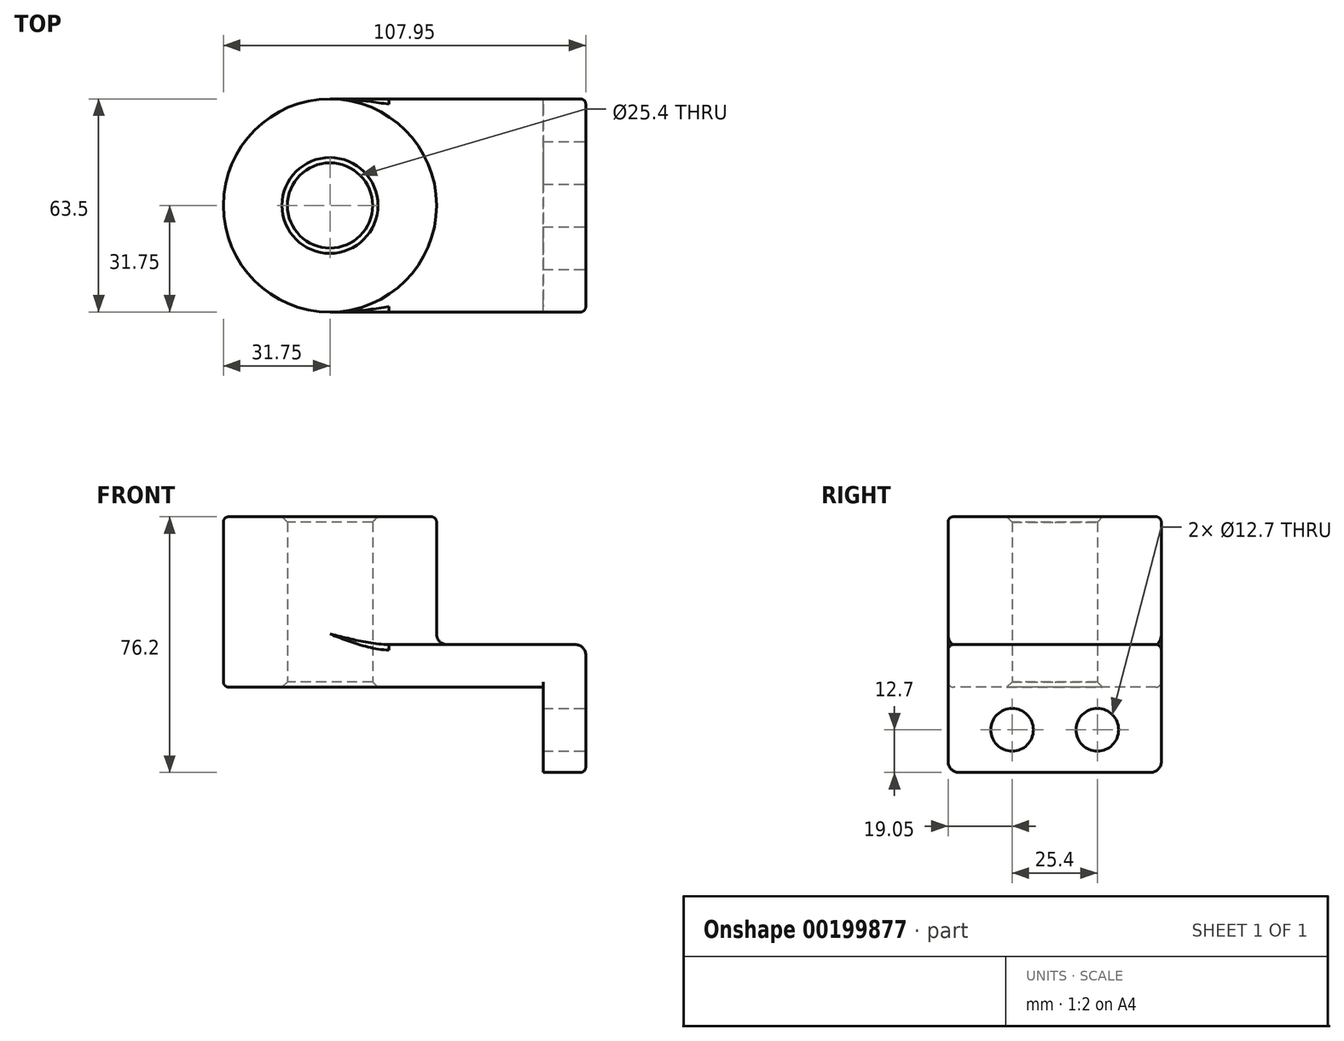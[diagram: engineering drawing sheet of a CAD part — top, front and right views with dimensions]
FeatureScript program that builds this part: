
annotation { "Feature Type Name" : "Feature", "Feature Type Description" : "" }
export const myFeature = defineFeature(function(context is Context, id is Id, definition is map)
    precondition{}
    {
        {
            var Q0;
            Q0=qCreatedBy(makeId("Top.planeOp"),FACE);
            var sketch = newSketch(context, id + "F0", { "sketchPlane" : qUnion([Q0])});
            skLineSegment(sketch, "E0.bottom", {"start": v(38.1, 31.75) * mm, "end": v(-38.1, 31.75) * mm});
            skLineSegment(sketch, "E0.top", {"start": v(38.1, -31.75) * mm, "end": v(-38.1, -31.75) * mm});
            skLineSegment(sketch, "E0.left", {"start": v(38.1, 31.75) * mm, "end": v(38.1, -31.75) * mm});
            skLineSegment(sketch, "E0.right", {"start": v(-38.1, 31.75) * mm, "end": v(-38.1, -31.75) * mm});
            skPoint(sketch, "E0.middle", {"position": v(0, 0) * mm});
            skCircle(sketch, "E1", {"center": v(-38.1, 0) * mm, "radius": 31.75 * mm});
            skCircle(sketch, "E2", {"center": v(-38.1, 0) * mm, "radius": 12.7 * mm});
            skSolve(sketch);
        }
        {
            var Q0;
            Q0 = qSketchRegion(id + "F0", true);
            extrude(context, id + "F1", {"entities" : qUnion([Q0]), "depth" : 12.7 * mm});
        }
        {
            var Q0;
            {var subQ1=sQuery(id+"F0.wireOp",EDGE,"E0.right");var subQ3=sQuery(id+"F0.wireOp",EDGE,"E2");var subQ4=makeQuery(id+"F0.imprint","INTERSECT",VERTEX,{"disambiguationData":[OD(0.0)],"derivedFrom":[subQ1,subQ3]});Q0=makeQuery(id+"F0.imprint","IMPRINT",FACE,{"disambiguationData":[TD([[makeQuery(id+"F0.imprint","IMPRINT",EDGE,{"disambiguationData":[TD([[subQ4,1.0]])],"derivedFrom":subQ3}),-1.0]])]});}
            var Q1;
            {var subQ1=sQuery(id+"F0.wireOp",EDGE,"E0.right");var subQ3=sQuery(id+"F0.wireOp",EDGE,"E2");var subQ4=makeQuery(id+"F0.imprint","INTERSECT",VERTEX,{"disambiguationData":[OD(0.0)],"derivedFrom":[subQ1,subQ3]});Q1=makeQuery(id+"F0.imprint","IMPRINT",FACE,{"disambiguationData":[TD([[makeQuery(id+"F0.imprint","IMPRINT",EDGE,{"disambiguationData":[TD([[subQ4,-1.0]])],"derivedFrom":subQ3}),-1.0]])]});}
            extrude(context, id + "F2", {"entities" : qUnion([Q0, Q1]), "operationType" : NewBodyOperationType.ADD, "depth" : 50.8 * mm});
        }
        {
            var Q0;
            Q0=makeQuery(id+"F1.opExtrude","SWEPT_FACE",FACE,{"disambiguationData":[OSD([sQuery(id+"F0.wireOp",EDGE,"E0.left")])]});
            var sketch = newSketch(context, id + "F3", { "sketchPlane" : qUnion([Q0])});
            skLineSegment(sketch, "E3.bottom", {"start": v(-31.75, 12.7) * mm, "end": v(31.75, 12.7) * mm});
            skLineSegment(sketch, "E3.top", {"start": v(-31.75, -25.4) * mm, "end": v(31.75, -25.4) * mm});
            skLineSegment(sketch, "E3.left", {"start": v(-31.75, 12.7) * mm, "end": v(-31.75, -25.4) * mm});
            skLineSegment(sketch, "E3.right", {"start": v(31.75, 12.7) * mm, "end": v(31.75, -25.4) * mm});
            skCircle(sketch, "E4", {"center": v(-12.7, -12.7) * mm, "radius": 6.35 * mm});
            skLineSegment(sketch, "E5", {"start": v(0, 0) * mm, "end": v(0, -25.4) * mm, "construction": true});
            skCircle(sketch, "E6.MirrorC", {"center": v(12.7, -12.7) * mm, "radius": 6.35 * mm});
            skSolve(sketch);
        }
        {
            var Q0;
            {var subQ2=sQuery(id+"F3.wireOp",EDGE,"E3.top");Q0=makeQuery(id+"F3.imprint","IMPRINT",FACE,{"disambiguationData":[TD([[makeQuery(id+"F3.imprint","IMPRINT",EDGE,{"derivedFrom":subQ2}),1.0]])]});}
            extrude(context, id + "F4", {"entities" : qUnion([Q0]), "operationType" : NewBodyOperationType.ADD, "oppositeDirection" : true, "depth" : 12.7 * mm});
        }
        {
            var Q0;
            {var subQ0=sQuery(id+"F0.wireOp",EDGE,"E1");Q0=makeQuery(id+"F2.boolean.opBoolean","INTERSECT",EDGE,{"derivedFrom":[makeQuery(id+"F1.opExtrude","CAP_FACE",FACE,{"disambiguationData":[OSD([sQuery(id+"F0.wireOp",EDGE,"E0.bottom"),sQuery(id+"F0.wireOp",EDGE,"E0.top"),sQuery(id+"F0.wireOp",EDGE,"E0.left"),subQ0,sQuery(id+"F0.wireOp",EDGE,"E2")])],"isStart":false}),makeQuery(id+"F2.opExtrude","SWEPT_FACE",FACE,{"disambiguationData":[OSD([subQ0])]})]});}
            var Q1;
            Q1=makeQuery(id+"F1.opExtrude","CAP_EDGE",EDGE,{"disambiguationData":[OSD([sQuery(id+"F0.wireOp",EDGE,"E0.left")])],"isStart":false});
            var Q2;
            Q2=makeQuery(id+"F4.opExtrude","SWEPT_EDGE",EDGE,{"disambiguationData":[OSD([sQuery(id+"F3.wireOp",EDGE,"E3.top"),sQuery(id+"F3.wireOp",EDGE,"E3.left")])]});
            var Q3;
            Q3=makeQuery(id+"F4.opExtrude","SWEPT_EDGE",EDGE,{"disambiguationData":[OSD([sQuery(id+"F3.wireOp",EDGE,"E3.top"),sQuery(id+"F3.wireOp",EDGE,"E3.right")])]});
            fillet(context, id + "F5", {"entities" : qUnion([Q0, Q1, Q2, Q3]), "radius" : 3.17 * mm, "tangentPropagation" : true, "allowEdgeOverflow" : false});
        }
        {
            var Q0;
            Q0=makeQuery(id+"F1.opExtrude","CAP_EDGE",EDGE,{"disambiguationData":[OSD([sQuery(id+"F0.wireOp",EDGE,"E0.top")])],"isStart":false});
            var Q1;
            Q1=makeQuery(id+"F1.opExtrude","CAP_EDGE",EDGE,{"disambiguationData":[OSD([sQuery(id+"F0.wireOp",EDGE,"E0.top")])],"isStart":true});
            var Q2;
            Q2=makeQuery(id+"F4.opExtrude","CAP_EDGE",EDGE,{"disambiguationData":[OSD([sQuery(id+"F0.wireOp",EDGE,"E0.left")])],"isStart":false});
            fillet(context, id + "F6", {"entities" : qUnion([Q0, Q1, Q2]), "radius" : 1.59 * mm, "tangentPropagation" : true, "allowEdgeOverflow" : false});
        }
        {
            var Q0;
            {var subQ0=sQuery(id+"F0.wireOp",EDGE,"E2");Q0=makeQuery(id+"F2.boolean.opBoolean","MERGE",FACE,{"derivedFrom":[makeQuery(id+"F1.opExtrude","SWEPT_FACE",FACE,{"disambiguationData":[OSD([subQ0])]}),makeQuery(id+"F2.opExtrude","SWEPT_FACE",FACE,{"disambiguationData":[OSD([subQ0])]})]});}
            chamfer(context, id + "F7", {"entities" : qUnion([Q0]), "width" : 1.59 * mm, "tangentPropagation" : true});
        }
        {
            var Q0;
            Q0=makeQuery(id+"F2.opExtrude","CAP_EDGE",EDGE,{"disambiguationData":[OSD([sQuery(id+"F0.wireOp",EDGE,"E1")])],"isStart":false});
            fillet(context, id + "F8", {"entities" : qUnion([Q0]), "radius" : 1.59 * mm, "tangentPropagation" : true, "allowEdgeOverflow" : false});
        }
    });
